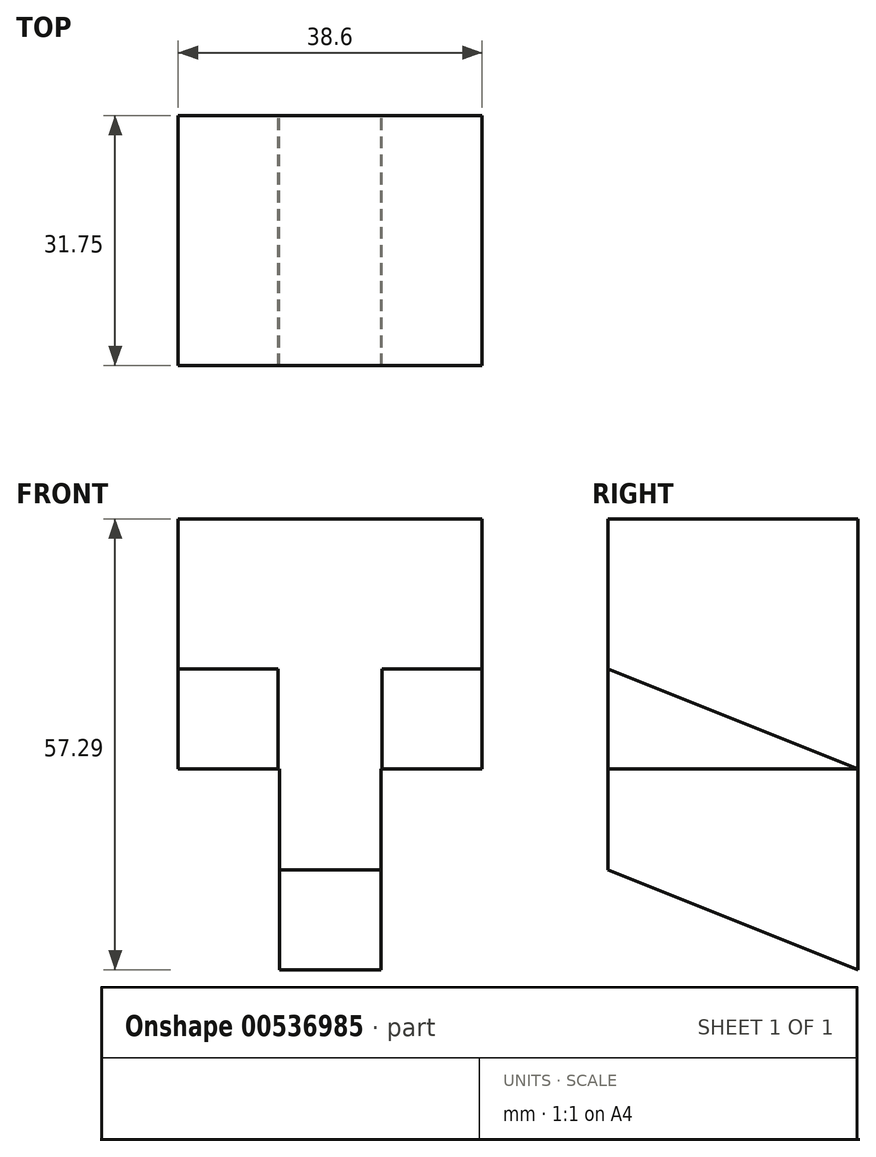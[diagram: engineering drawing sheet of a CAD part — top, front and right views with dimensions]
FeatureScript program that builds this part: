
annotation { "Feature Type Name" : "Feature", "Feature Type Description" : "" }
export const myFeature = defineFeature(function(context is Context, id is Id, definition is map)
    precondition{}
    {
        {
            var Q0;
            Q0=qCreatedBy(makeId("Front.planeOp"),FACE);
            var sketch = newSketch(context, id + "F0", { "sketchPlane" : qUnion([Q0])});
            skLineSegment(sketch, "E0", {"start": v(-56.39, 49.35) * mm, "end": v(-56.39, 17.6) * mm});
            skLineSegment(sketch, "E1", {"start": v(-56.39, 17.6) * mm, "end": v(-43.52, 17.6) * mm});
            skLineSegment(sketch, "E2", {"start": v(-43.52, 17.6) * mm, "end": v(-43.52, -7.94) * mm});
            skLineSegment(sketch, "E3", {"start": v(-43.52, -7.94) * mm, "end": v(-30.66, -7.94) * mm});
            skLineSegment(sketch, "E4", {"start": v(-30.66, -7.94) * mm, "end": v(-30.66, 17.6) * mm});
            skLineSegment(sketch, "E5", {"start": v(-30.66, 17.6) * mm, "end": v(-17.8, 17.6) * mm});
            skLineSegment(sketch, "E6", {"start": v(-17.8, 17.6) * mm, "end": v(-17.8, 49.35) * mm});
            skLineSegment(sketch, "E7", {"start": v(-17.8, 49.35) * mm, "end": v(-56.39, 49.35) * mm});
            skSolve(sketch);
        }
        {
            var Q0;
            Q0=makeQuery(id+"F0.imprint","IMPRINT",FACE,{"disambiguationData":[TD([[makeQuery(id+"F0.imprint","IMPRINT",EDGE,{"derivedFrom":sQuery(id+"F0.wireOp",EDGE,"E0")}),1.0]])]});
            extrude(context, id + "F1", {"entities" : qUnion([Q0]), "depth" : 31.75 * mm, "offsetDistance" : 25.4 * mm});
        }
        {
            var Q0;
            Q0=makeQuery(id+"F1.opExtrude","SWEPT_FACE",FACE,{"disambiguationData":[OSD([sQuery(id+"F0.wireOp",EDGE,"E4")])]});
            var sketch = newSketch(context, id + "F2", { "sketchPlane" : qUnion([Q0])});
            skLineSegment(sketch, "E8", {"start": v(-31.75, 4.76) * mm, "end": v(0, -7.94) * mm});
            skSolve(sketch);
        }
        {
            var Q0;
            {var subQ0=sQuery(id+"F2.wireOp",EDGE,"E8");Q0=makeQuery(id+"F2.imprint","IMPRINT",FACE,{"disambiguationData":[TD([[makeQuery(id+"F2.imprint","IMPRINT",EDGE,{"derivedFrom":subQ0}),-1.0]])]});}
            extrude(context, id + "F3", {"entities" : qUnion([Q0]), "operationType" : NewBodyOperationType.REMOVE, "endBound" : BoundingType.THROUGH_ALL, "oppositeDirection" : true, "depth" : 25.4 * mm, "offsetDistance" : 25.4 * mm});
        }
        {
            var Q0;
            Q0=makeQuery(id+"F1.opExtrude","SWEPT_FACE",FACE,{"disambiguationData":[OSD([sQuery(id+"F0.wireOp",EDGE,"E0")])]});
            var sketch = newSketch(context, id + "F4", { "sketchPlane" : qUnion([Q0])});
            skLineSegment(sketch, "E9", {"start": v(31.75, 30.3) * mm, "end": v(0, 17.6) * mm});
            skSolve(sketch);
        }
        {
            var Q0;
            {var subQ0=sQuery(id+"F4.wireOp",EDGE,"E9");Q0=makeQuery(id+"F4.imprint","IMPRINT",FACE,{"disambiguationData":[TD([[makeQuery(id+"F4.imprint","IMPRINT",EDGE,{"derivedFrom":subQ0}),1.0]])]});}
            extrude(context, id + "F5", {"entities" : qUnion([Q0]), "operationType" : NewBodyOperationType.REMOVE, "oppositeDirection" : true, "depth" : 12.7 * mm, "offsetDistance" : 25.4 * mm});
        }
        {
            var Q0;
            Q0=makeQuery(id+"F1.opExtrude","SWEPT_FACE",FACE,{"disambiguationData":[OSD([sQuery(id+"F0.wireOp",EDGE,"E6")])]});
            var sketch = newSketch(context, id + "F6", { "sketchPlane" : qUnion([Q0])});
            skLineSegment(sketch, "E10", {"start": v(-31.75, 30.3) * mm, "end": v(0, 17.6) * mm});
            skSolve(sketch);
        }
        {
            var Q0;
            {var subQ0=sQuery(id+"F6.wireOp",EDGE,"E10");Q0=makeQuery(id+"F6.imprint","IMPRINT",FACE,{"disambiguationData":[TD([[makeQuery(id+"F6.imprint","IMPRINT",EDGE,{"derivedFrom":subQ0}),-1.0]])]});}
            extrude(context, id + "F7", {"entities" : qUnion([Q0]), "operationType" : NewBodyOperationType.REMOVE, "oppositeDirection" : true, "depth" : 12.7 * mm, "offsetDistance" : 25.4 * mm});
        }
    });
